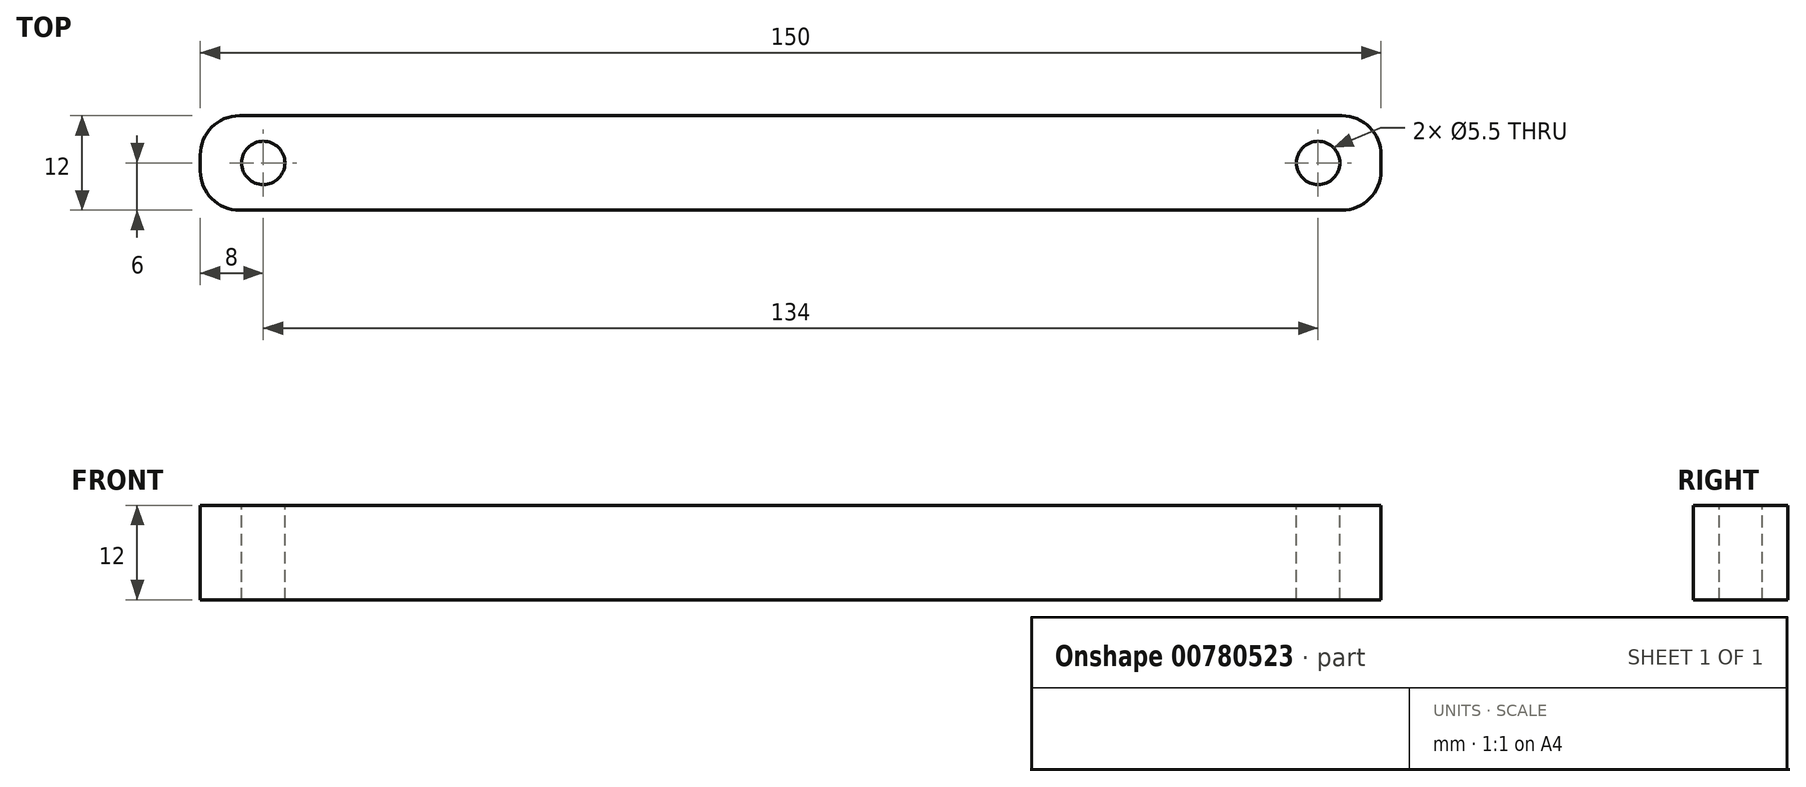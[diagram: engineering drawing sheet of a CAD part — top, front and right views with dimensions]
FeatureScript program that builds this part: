
annotation { "Feature Type Name" : "Feature", "Feature Type Description" : "" }
export const myFeature = defineFeature(function(context is Context, id is Id, definition is map)
    precondition{}
    {
        {
            var Q0;
            Q0=qCreatedBy(makeId("Top.planeOp"),FACE);
            var sketch = newSketch(context, id + "F0", { "sketchPlane" : qUnion([Q0])});
            skLineSegment(sketch, "E0.bottom", {"start": v(-75, 6) * mm, "end": v(75, 6) * mm});
            skLineSegment(sketch, "E0.top", {"start": v(-75, -6) * mm, "end": v(75, -6) * mm});
            skLineSegment(sketch, "E0.left", {"start": v(-75, 6) * mm, "end": v(-75, -6) * mm});
            skLineSegment(sketch, "E0.right", {"start": v(75, 6) * mm, "end": v(75, -6) * mm});
            skSolve(sketch);
        }
        {
            var Q0;
            Q0=makeQuery(id+"F0.imprint","IMPRINT",FACE,{"disambiguationData":[TD([[makeQuery(id+"F0.imprint","IMPRINT",EDGE,{"derivedFrom":sQuery(id+"F0.wireOp",EDGE,"E0.bottom")}),-1.0]])]});
            extrude(context, id + "F1", {"entities" : qUnion([Q0]), "depth" : 12 * mm, "offsetDistance" : 25 * mm});
        }
        {
            var Q0;
            Q0=makeQuery(id+"F1.opExtrude","CAP_FACE",FACE,{"disambiguationData":[OSD([sQuery(id+"F0.wireOp",EDGE,"E0.bottom"),sQuery(id+"F0.wireOp",EDGE,"E0.top"),sQuery(id+"F0.wireOp",EDGE,"E0.left"),sQuery(id+"F0.wireOp",EDGE,"E0.right")])],"isStart":false});
            var sketch = newSketch(context, id + "F2", { "sketchPlane" : qUnion([Q0])});
            skPoint(sketch, "E1", {"position": v(-67, 0) * mm});
            skPoint(sketch, "E2", {"position": v(67, 0) * mm});
            skSolve(sketch);
        }
        {
            var Q0;
            Q0=sQuery(id+"F2.wireOp",VERTEX,"E2");
            var Q1;
            Q1=sQuery(id+"F2.wireOp",VERTEX,"E1");
            var Q2;
            Q2=makeQuery(id+"F1.opExtrude","SWEPT_BODY",BODY,{"disambiguationData":[OSD([sQuery(id+"F0.wireOp",EDGE,"E0.bottom"),sQuery(id+"F0.wireOp",EDGE,"E0.top"),sQuery(id+"F0.wireOp",EDGE,"E0.left"),sQuery(id+"F0.wireOp",EDGE,"E0.right")])]});
            hole(context, id + "F3", {"style" : HoleStyle.SIMPLE, "endStyle" : HoleEndStyle.THROUGH, "standardTappedOrClearance" : lookupTablePath({ "standard" : "ISO", "fit" : "Normal", "size" : "M5", "type" : "Clearance" }), "standardBlindInLast" : lookupTablePath({ "fit" : "Standard", "standard" : "ISO", "size" : "M5", "type" : "Clearance" }), "holeDiameter" : 5.5 * mm, "majorDiameter" : 5 * mm, "isTappedThrough" : true, "tappedDepth" : 12 * mm, "tapClearance" : 3, "locations" : qUnion([Q0, Q1]), "scope" : qUnion([Q2])});
        }
        {
            var Q0;
            Q0=makeQuery(id+"F1.opExtrude","SWEPT_EDGE",EDGE,{"disambiguationData":[OSD([sQuery(id+"F0.wireOp",EDGE,"E0.top"),sQuery(id+"F0.wireOp",EDGE,"E0.left")])]});
            var Q1;
            Q1=makeQuery(id+"F1.opExtrude","SWEPT_EDGE",EDGE,{"disambiguationData":[OSD([sQuery(id+"F0.wireOp",EDGE,"E0.bottom"),sQuery(id+"F0.wireOp",EDGE,"E0.left")])]});
            var Q2;
            Q2=makeQuery(id+"F1.opExtrude","SWEPT_EDGE",EDGE,{"disambiguationData":[OSD([sQuery(id+"F0.wireOp",EDGE,"E0.top"),sQuery(id+"F0.wireOp",EDGE,"E0.right")])]});
            var Q3;
            Q3=makeQuery(id+"F1.opExtrude","SWEPT_EDGE",EDGE,{"disambiguationData":[OSD([sQuery(id+"F0.wireOp",EDGE,"E0.bottom"),sQuery(id+"F0.wireOp",EDGE,"E0.right")])]});
            fillet(context, id + "F4", {"entities" : qUnion([Q0, Q1, Q2, Q3]), "radius" : 5 * mm, "tangentPropagation" : true, "allowEdgeOverflow" : false});
        }
    });
